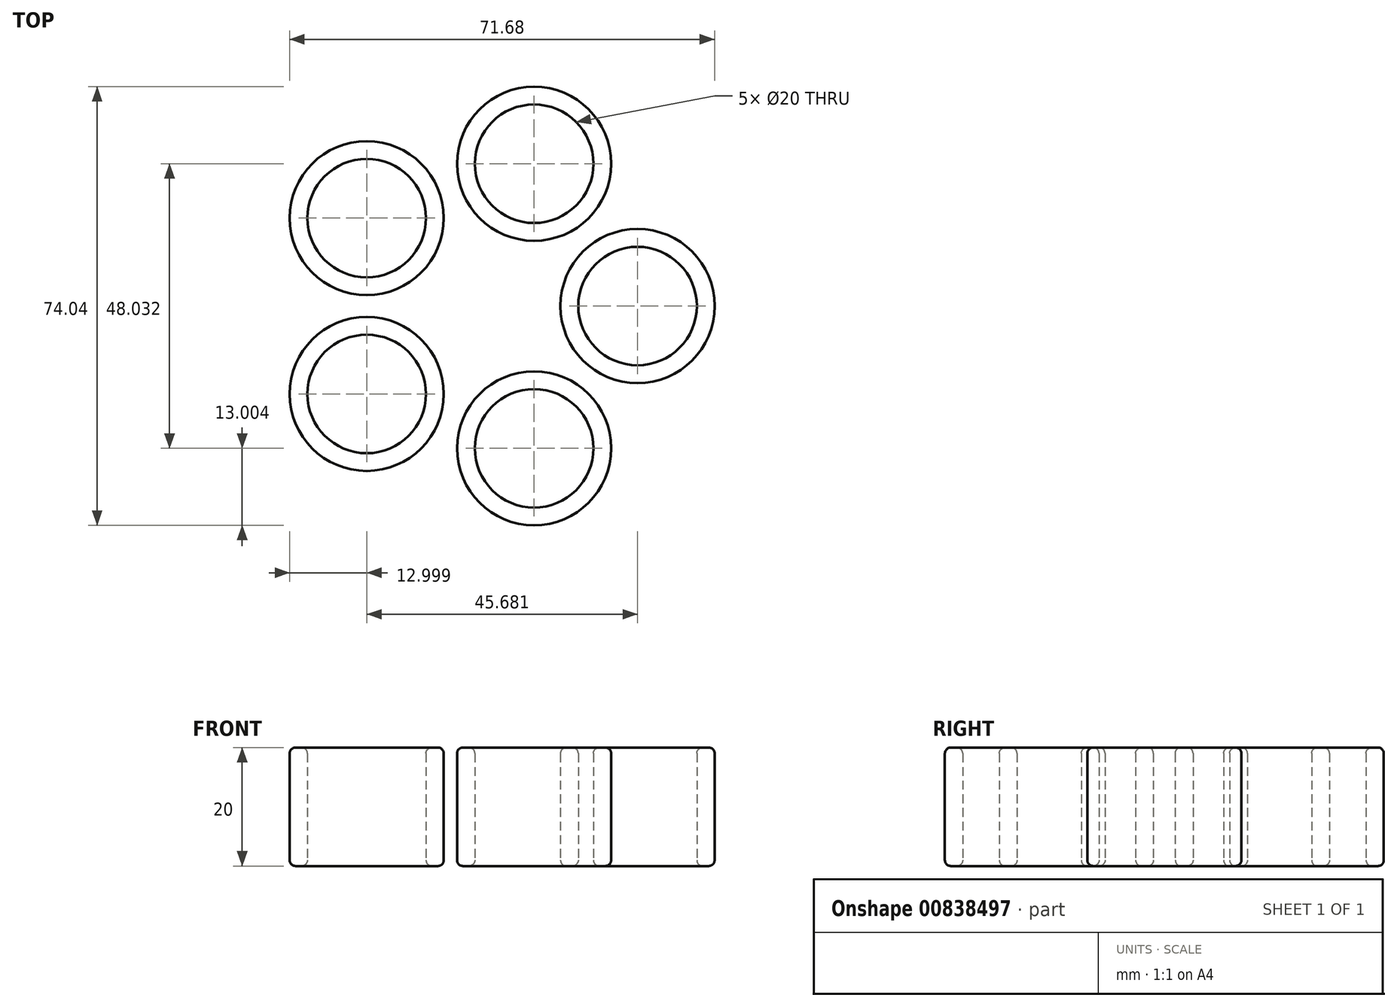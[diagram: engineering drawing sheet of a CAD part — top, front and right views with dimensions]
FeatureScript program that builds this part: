
annotation { "Feature Type Name" : "Feature", "Feature Type Description" : "" }
export const myFeature = defineFeature(function(context is Context, id is Id, definition is map)
    precondition{}
    {
        {
            var Q0;
            Q0=qCreatedBy(makeId("Front.planeOp"),FACE);
            var sketch = newSketch(context, id + "F0", { "sketchPlane" : qUnion([Q0])});
            skLineSegment(sketch, "E0", {"start": v(-13, 24.07) * mm, "end": v(-13, 4.07) * mm});
            skLineSegment(sketch, "E1", {"start": v(-10, 4.07) * mm, "end": v(-10, 24.07) * mm});
            skLineSegment(sketch, "E2", {"start": v(-10, 24.07) * mm, "end": v(-13, 24.07) * mm});
            skLineSegment(sketch, "E3", {"start": v(-13, 4.07) * mm, "end": v(-10, 4.07) * mm});
            skLineSegment(sketch, "E4", {"start": v(0, 0) * mm, "end": v(0, 1) * mm});
            skLineSegment(sketch, "E5", {"start": v(-25.25, -8.55) * mm, "end": v(-25.25, -9.55) * mm});
            skSolve(sketch);
        }
        {
            var Q0;
            Q0 = qSketchRegion(id + "F0", true);
            var Q1;
            Q1=sQuery(id+"F0.wireOp",EDGE,"E4");
            revolve(context, id + "F1", {"surfaceOperationType" : NewSurfaceOperationType.NEW, "entities" : qUnion([Q0]), "axis" : qUnion([Q1]), "revolveType" : RevolveType.FULL});
        }
        {
            var Q0;
            Q0=makeQuery(id+"F1.opRevolve","SWEPT_BODY",BODY,{"disambiguationData":[OSD([sQuery(id+"F0.wireOp",EDGE,"E0"),sQuery(id+"F0.wireOp",EDGE,"E1"),sQuery(id+"F0.wireOp",EDGE,"E2"),sQuery(id+"F0.wireOp",EDGE,"E3")])]});
            var Q1;
            Q1=sQuery(id+"F0.wireOp",EDGE,"E5");
            circularPattern(context, id + "F2", {"entities" : qUnion([Q0]), "axis" : qUnion([Q1]), "angle" : 360 * degree, "instanceCount" : 5, "equalSpace" : true});
        }
        {
            var Q0;
            Q0=makeQuery(id+"F2.opPattern","COPY",EDGE,{"derivedFrom":makeQuery(id+"F1.opRevolve","SWEPT_EDGE",EDGE,{"disambiguationData":[OSD([sQuery(id+"F0.wireOp",EDGE,"E1"),sQuery(id+"F0.wireOp",EDGE,"E2")])]}),"instanceName":"4"});
            fillet(context, id + "F3", {"entities" : qUnion([Q0]), "radius" : 1 * mm, "tangentPropagation" : true, "allowEdgeOverflow" : false});
        }
        {
            var Q0;
            Q0=makeQuery(id+"F2.opPattern","COPY",EDGE,{"derivedFrom":makeQuery(id+"F1.opRevolve","SWEPT_EDGE",EDGE,{"disambiguationData":[OSD([sQuery(id+"F0.wireOp",EDGE,"E0"),sQuery(id+"F0.wireOp",EDGE,"E2")])]}),"instanceName":"4"});
            fillet(context, id + "F4", {"entities" : qUnion([Q0]), "radius" : 1 * mm, "tangentPropagation" : true, "allowEdgeOverflow" : false});
        }
        {
            var Q0;
            Q0=makeQuery(id+"F1.opRevolve","SWEPT_FACE",FACE,{"disambiguationData":[OSD([sQuery(id+"F0.wireOp",EDGE,"E0")])]});
            var Q1;
            Q1=makeQuery(id+"F2.opPattern","COPY",EDGE,{"derivedFrom":makeQuery(id+"F1.opRevolve","SWEPT_EDGE",EDGE,{"disambiguationData":[OSD([sQuery(id+"F0.wireOp",EDGE,"E0"),sQuery(id+"F0.wireOp",EDGE,"E3")])]}),"instanceName":"4"});
            var Q2;
            Q2=makeQuery(id+"F2.opPattern","COPY",EDGE,{"derivedFrom":makeQuery(id+"F1.opRevolve","SWEPT_EDGE",EDGE,{"disambiguationData":[OSD([sQuery(id+"F0.wireOp",EDGE,"E1"),sQuery(id+"F0.wireOp",EDGE,"E3")])]}),"instanceName":"4"});
            var Q3;
            Q3=makeQuery(id+"F2.opPattern","COPY",EDGE,{"derivedFrom":makeQuery(id+"F1.opRevolve","SWEPT_EDGE",EDGE,{"disambiguationData":[OSD([sQuery(id+"F0.wireOp",EDGE,"E0"),sQuery(id+"F0.wireOp",EDGE,"E3")])]}),"instanceName":"3"});
            var Q4;
            Q4=makeQuery(id+"F2.opPattern","COPY",EDGE,{"derivedFrom":makeQuery(id+"F1.opRevolve","SWEPT_EDGE",EDGE,{"disambiguationData":[OSD([sQuery(id+"F0.wireOp",EDGE,"E1"),sQuery(id+"F0.wireOp",EDGE,"E3")])]}),"instanceName":"3"});
            var Q5;
            Q5=makeQuery(id+"F2.opPattern","COPY",EDGE,{"derivedFrom":makeQuery(id+"F1.opRevolve","SWEPT_EDGE",EDGE,{"disambiguationData":[OSD([sQuery(id+"F0.wireOp",EDGE,"E0"),sQuery(id+"F0.wireOp",EDGE,"E3")])]}),"instanceName":"2"});
            var Q6;
            Q6=makeQuery(id+"F2.opPattern","COPY",EDGE,{"derivedFrom":makeQuery(id+"F1.opRevolve","SWEPT_EDGE",EDGE,{"disambiguationData":[OSD([sQuery(id+"F0.wireOp",EDGE,"E1"),sQuery(id+"F0.wireOp",EDGE,"E3")])]}),"instanceName":"2"});
            var Q7;
            Q7=makeQuery(id+"F2.opPattern","COPY",EDGE,{"derivedFrom":makeQuery(id+"F1.opRevolve","SWEPT_EDGE",EDGE,{"disambiguationData":[OSD([sQuery(id+"F0.wireOp",EDGE,"E0"),sQuery(id+"F0.wireOp",EDGE,"E3")])]}),"instanceName":"1"});
            var Q8;
            Q8=makeQuery(id+"F2.opPattern","COPY",EDGE,{"derivedFrom":makeQuery(id+"F1.opRevolve","SWEPT_EDGE",EDGE,{"disambiguationData":[OSD([sQuery(id+"F0.wireOp",EDGE,"E1"),sQuery(id+"F0.wireOp",EDGE,"E3")])]}),"instanceName":"1"});
            fillet(context, id + "F5", {"entities" : qUnion([Q0, Q1, Q2, Q3, Q4, Q5, Q6, Q7, Q8]), "radius" : 1 * mm, "tangentPropagation" : true, "allowEdgeOverflow" : false});
        }
        {
            var Q0;
            Q0=makeQuery(id+"F1.opRevolve","SWEPT_EDGE",EDGE,{"disambiguationData":[OSD([sQuery(id+"F0.wireOp",EDGE,"E1"),sQuery(id+"F0.wireOp",EDGE,"E2")])]});
            var Q1;
            Q1=makeQuery(id+"F2.opPattern","COPY",EDGE,{"derivedFrom":makeQuery(id+"F1.opRevolve","SWEPT_EDGE",EDGE,{"disambiguationData":[OSD([sQuery(id+"F0.wireOp",EDGE,"E1"),sQuery(id+"F0.wireOp",EDGE,"E2")])]}),"instanceName":"1"});
            var Q2;
            Q2=makeQuery(id+"F2.opPattern","COPY",EDGE,{"derivedFrom":makeQuery(id+"F1.opRevolve","SWEPT_EDGE",EDGE,{"disambiguationData":[OSD([sQuery(id+"F0.wireOp",EDGE,"E0"),sQuery(id+"F0.wireOp",EDGE,"E2")])]}),"instanceName":"1"});
            var Q3;
            Q3=makeQuery(id+"F2.opPattern","COPY",EDGE,{"derivedFrom":makeQuery(id+"F1.opRevolve","SWEPT_EDGE",EDGE,{"disambiguationData":[OSD([sQuery(id+"F0.wireOp",EDGE,"E0"),sQuery(id+"F0.wireOp",EDGE,"E2")])]}),"instanceName":"2"});
            var Q4;
            Q4=makeQuery(id+"F2.opPattern","COPY",EDGE,{"derivedFrom":makeQuery(id+"F1.opRevolve","SWEPT_EDGE",EDGE,{"disambiguationData":[OSD([sQuery(id+"F0.wireOp",EDGE,"E1"),sQuery(id+"F0.wireOp",EDGE,"E2")])]}),"instanceName":"2"});
            var Q5;
            Q5=makeQuery(id+"F2.opPattern","COPY",EDGE,{"derivedFrom":makeQuery(id+"F1.opRevolve","SWEPT_EDGE",EDGE,{"disambiguationData":[OSD([sQuery(id+"F0.wireOp",EDGE,"E0"),sQuery(id+"F0.wireOp",EDGE,"E2")])]}),"instanceName":"3"});
            var Q6;
            Q6=makeQuery(id+"F2.opPattern","COPY",EDGE,{"derivedFrom":makeQuery(id+"F1.opRevolve","SWEPT_EDGE",EDGE,{"disambiguationData":[OSD([sQuery(id+"F0.wireOp",EDGE,"E1"),sQuery(id+"F0.wireOp",EDGE,"E2")])]}),"instanceName":"3"});
            fillet(context, id + "F6", {"entities" : qUnion([Q0, Q1, Q2, Q3, Q4, Q5, Q6]), "radius" : 1 * mm, "tangentPropagation" : true, "allowEdgeOverflow" : false});
        }
        {
            var Q0;
            Q0=makeQuery(id+"F1.opRevolve","SWEPT_EDGE",EDGE,{"disambiguationData":[OSD([sQuery(id+"F0.wireOp",EDGE,"E1"),sQuery(id+"F0.wireOp",EDGE,"E3")])]});
            fillet(context, id + "F7", {"entities" : qUnion([Q0]), "radius" : 1 * mm, "tangentPropagation" : true, "allowEdgeOverflow" : false});
        }
    });
